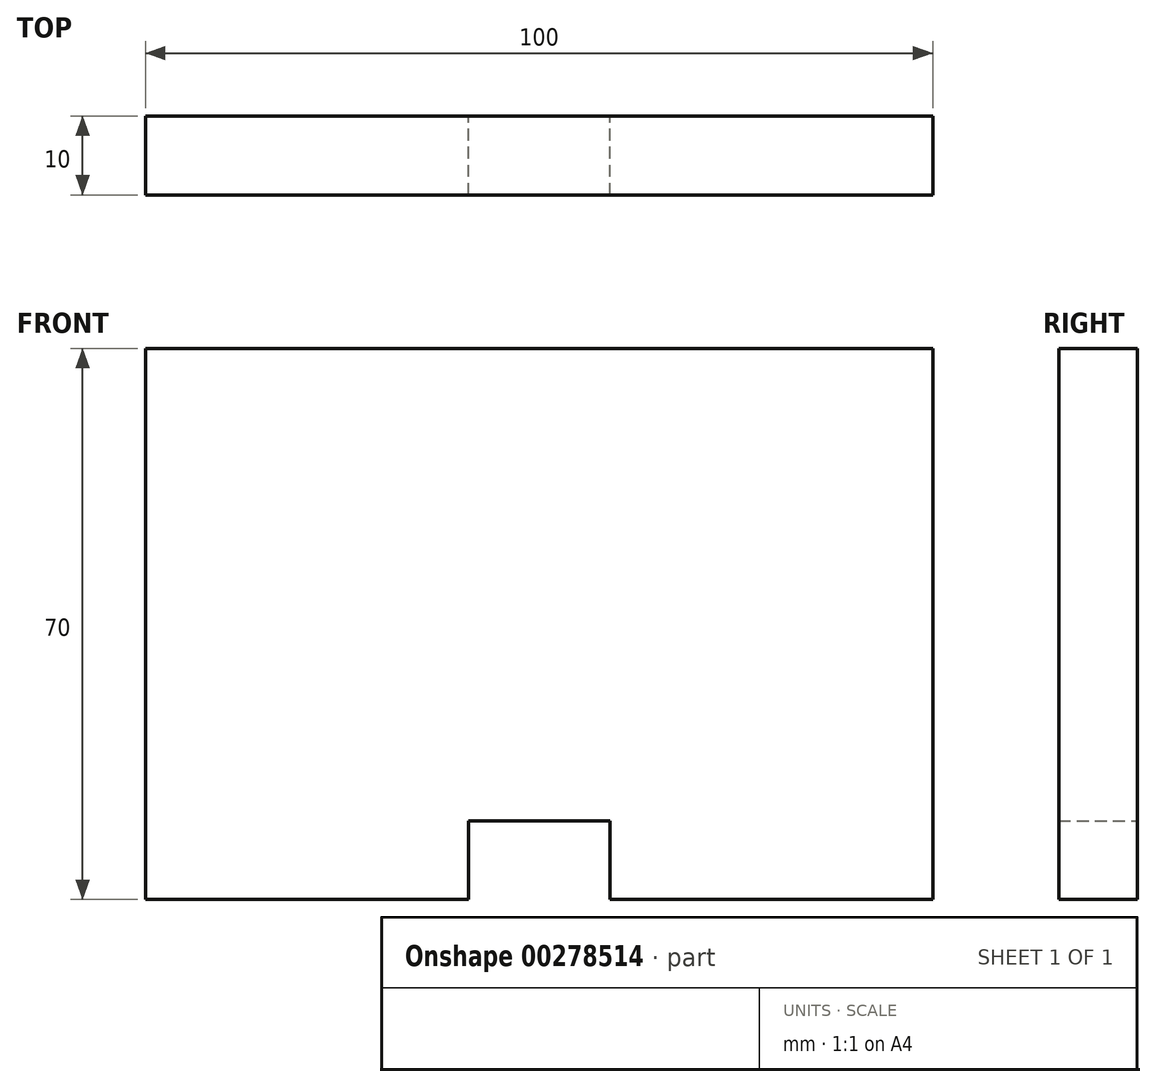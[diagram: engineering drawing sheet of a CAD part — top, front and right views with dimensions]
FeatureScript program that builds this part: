
annotation { "Feature Type Name" : "Feature", "Feature Type Description" : "" }
export const myFeature = defineFeature(function(context is Context, id is Id, definition is map)
    precondition{}
    {
        {
            var Q0;
            Q0=qCreatedBy(makeId("Front.planeOp"),FACE);
            var sketch = newSketch(context, id + "F0", { "sketchPlane" : qUnion([Q0])});
            skLineSegment(sketch, "E0.bottom", {"start": v(-50, 70) * mm, "end": v(50, 70) * mm});
            skLineSegment(sketch, "E0.top", {"start": v(-50, 0) * mm, "end": v(50, 0) * mm});
            skLineSegment(sketch, "E0.left", {"start": v(-50, 70) * mm, "end": v(-50, 0) * mm});
            skLineSegment(sketch, "E0.right", {"start": v(50, 70) * mm, "end": v(50, 0) * mm});
            skPoint(sketch, "E0.middle", {"position": v(0, 0) * mm});
            skSolve(sketch);
        }
        {
            var Q0;
            Q0=makeQuery(id+"F0.imprint","IMPRINT",FACE,{"disambiguationData":[TD([[makeQuery(id+"F0.imprint","IMPRINT",EDGE,{"derivedFrom":sQuery(id+"F0.wireOp",EDGE,"E0.bottom")}),-1.0]])]});
            extrude(context, id + "F1", {"entities" : qUnion([Q0]), "depth" : 10 * mm, "offsetDistance" : 25 * mm});
        }
        {
            var Q0;
            Q0=makeQuery(id+"F1.opExtrude","CAP_FACE",FACE,{"disambiguationData":[OSD([sQuery(id+"F0.wireOp",EDGE,"E0.bottom"),sQuery(id+"F0.wireOp",EDGE,"E0.top"),sQuery(id+"F0.wireOp",EDGE,"E0.left"),sQuery(id+"F0.wireOp",EDGE,"E0.right")])],"isStart":true});
            var sketch = newSketch(context, id + "F2", { "sketchPlane" : qUnion([Q0])});
            skPoint(sketch, "E1", {"position": v(0, 10) * mm});
            skArc(sketch, "E2.0", {"start": v(-3.75, 7) * mm, "mid": v(-3.6, 6.65) * mm, "end": v(-3.25, 6.5) * mm});
            skLineSegment(sketch, "E2.1", {"start": v(-3.75, 8.54) * mm, "end": v(-3.75, 7) * mm});
            skLineSegment(sketch, "E2.2", {"start": v(3.46, 8.82) * mm, "end": v(2.81, 9.78) * mm});
            skArc(sketch, "E2.3", {"start": v(3.55, 8.54) * mm, "mid": v(3.53, 8.68) * mm, "end": v(3.46, 8.82) * mm});
            skLineSegment(sketch, "E2.4", {"start": v(3.55, 7) * mm, "end": v(3.55, 8.54) * mm});
            skArc(sketch, "E2.5", {"start": v(3.05, 6.5) * mm, "mid": v(3.4, 6.65) * mm, "end": v(3.55, 7) * mm});
            skArc(sketch, "E2.6", {"start": v(2.81, 9.78) * mm, "mid": v(2.63, 9.94) * mm, "end": v(2.4, 10) * mm});
            skLineSegment(sketch, "E2.7", {"start": v(2.4, 10) * mm, "end": v(0, 10) * mm});
            skLineSegment(sketch, "E2.8", {"start": v(-3.25, 6.5) * mm, "end": v(3.05, 6.5) * mm});
            skLineSegment(sketch, "E2.9", {"start": v(0, 10) * mm, "end": v(-2.6, 10) * mm});
            skArc(sketch, "E2.10", {"start": v(-2.6, 10) * mm, "mid": v(-2.84, 9.94) * mm, "end": v(-3.02, 9.78) * mm});
            skLineSegment(sketch, "E2.11", {"start": v(-3.02, 9.78) * mm, "end": v(-3.66, 8.82) * mm});
            skArc(sketch, "E2.12", {"start": v(-3.66, 8.82) * mm, "mid": v(-3.73, 8.68) * mm, "end": v(-3.75, 8.54) * mm});
            skLineSegment(sketch, "E3", {"start": v(0, 10) * mm, "end": v(-9, 10) * mm});
            skLineSegment(sketch, "E4.MirrorCS", {"start": v(0, 10) * mm, "end": v(9, 10) * mm});
            skLineSegment(sketch, "E5", {"start": v(-9, 10) * mm, "end": v(-15, 10) * mm});
            skLineSegment(sketch, "E6.MirrorCS", {"start": v(9, 10) * mm, "end": v(15, 10) * mm});
            skLineSegment(sketch, "E7", {"start": v(-15, 10) * mm, "end": v(-15, 0) * mm});
            skLineSegment(sketch, "E8", {"start": v(-9, 10) * mm, "end": v(-9, 0) * mm});
            skLineSegment(sketch, "E9.MirrorCS", {"start": v(15, 10) * mm, "end": v(15, 0) * mm});
            skLineSegment(sketch, "E10.MirrorCS", {"start": v(9, 10) * mm, "end": v(9, 0) * mm});
            skSolve(sketch);
        }
        {
            var Q0;
            Q0=makeQuery(id+"F2.imprint","IMPRINT",FACE,{"disambiguationData":[TD([[makeQuery(id+"F2.imprint","IMPRINT",EDGE,{"derivedFrom":sQuery(id+"F2.wireOp",EDGE,"E2.0")}),-1.0]])]});
            var Q1;
            Q1=makeQuery(id+"F2.imprint","IMPRINT",FACE,{"disambiguationData":[TD([[makeQuery(id+"F2.imprint","IMPRINT",EDGE,{"derivedFrom":sQuery(id+"F2.wireOp",EDGE,"E2.0")}),1.0]])]});
            extrude(context, id + "F3", {"entities" : qUnion([Q0, Q1]), "operationType" : NewBodyOperationType.REMOVE, "endBound" : BoundingType.UP_TO_NEXT, "oppositeDirection" : true, "depth" : 25 * mm, "offsetDistance" : 25 * mm});
        }
    });
